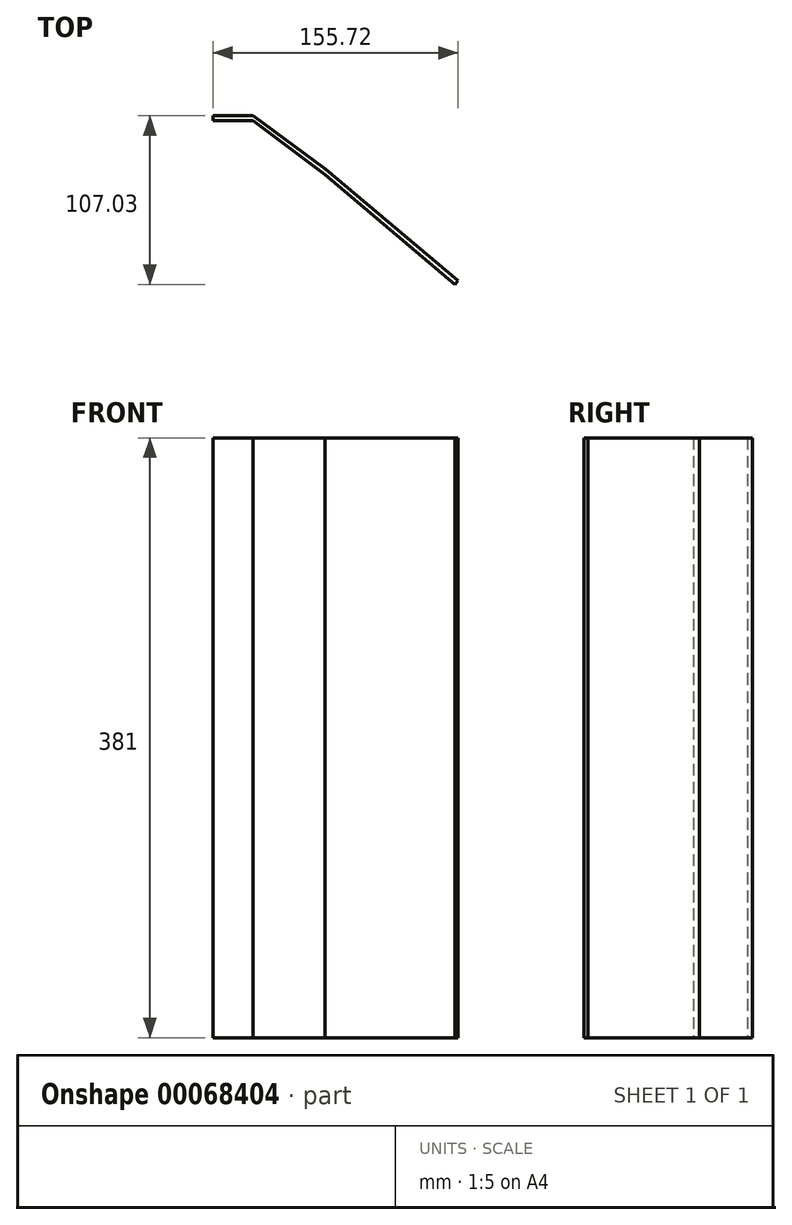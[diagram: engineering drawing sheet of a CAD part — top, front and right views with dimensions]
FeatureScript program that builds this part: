
annotation { "Feature Type Name" : "Feature", "Feature Type Description" : "" }
export const myFeature = defineFeature(function(context is Context, id is Id, definition is map)
    precondition{}
    {
        {
            var Q0;
            Q0=qCreatedBy(makeId("Top.planeOp"),FACE);
            var sketch = newSketch(context, id + "F0", { "sketchPlane" : qUnion([Q0])});
            skLineSegment(sketch, "E0", {"start": v(0, 0) * mm, "end": v(-82.55, 69.56) * mm});
            skLineSegment(sketch, "E1", {"start": v(-82.55, 69.56) * mm, "end": v(-128.27, 103.85) * mm});
            skLineSegment(sketch, "E2", {"start": v(-128.27, 103.85) * mm, "end": v(-153.67, 103.85) * mm});
            skLineSegment(sketch, "E3", {"start": v(2.05, 2.43) * mm, "end": v(0, 0) * mm});
            skLineSegment(sketch, "E4", {"start": v(2.05, 2.43) * mm, "end": v(-82.1, 73.34) * mm});
            skLineSegment(sketch, "E5", {"start": v(-82.1, 73.34) * mm, "end": v(-128.27, 107.03) * mm});
            skLineSegment(sketch, "E6", {"start": v(-128.27, 107.03) * mm, "end": v(-153.67, 107.03) * mm});
            skLineSegment(sketch, "E7", {"start": v(-153.67, 107.03) * mm, "end": v(-153.67, 103.85) * mm});
            skSolve(sketch);
        }
        {
            var Q0;
            Q0 = qSketchRegion(id + "F0", true);
            extrude(context, id + "F1", {"entities" : qUnion([Q0]), "depth" : 381 * mm});
        }
    });
